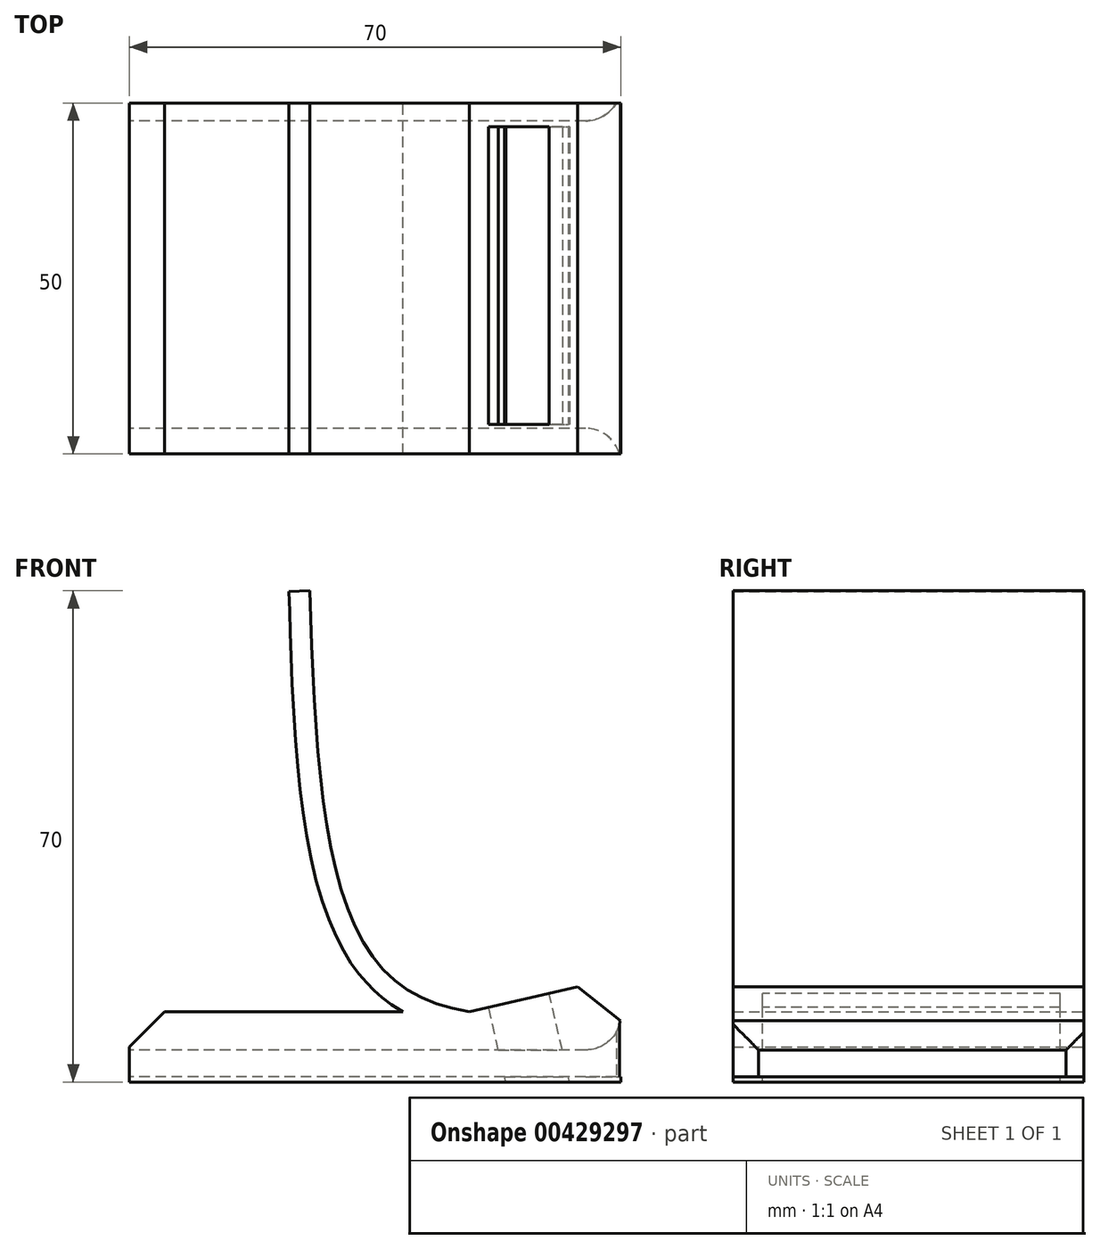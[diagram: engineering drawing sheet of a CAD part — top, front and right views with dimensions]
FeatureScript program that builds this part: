
annotation { "Feature Type Name" : "Feature", "Feature Type Description" : "" }
export const myFeature = defineFeature(function(context is Context, id is Id, definition is map)
    precondition{}
    {
        {
            var Q0;
            Q0=qCreatedBy(makeId("Front.planeOp"),FACE);
            var sketch = newSketch(context, id + "F0", { "sketchPlane" : qUnion([Q0])});
            skLineSegment(sketch, "E0.bottom", {"start": v(0, 0) * mm, "end": v(70, 0) * mm});
            skLineSegment(sketch, "E0.left", {"start": v(0, 0) * mm, "end": v(0, 10) * mm});
            skLineSegment(sketch, "E0.right", {"start": v(70, 0) * mm, "end": v(70, 14.95) * mm});
            skLineSegment(sketch, "E1.top", {"start": v(0, 10) * mm, "end": v(39.04, 10) * mm});
            skLineSegment(sketch, "E1.right", {"start": v(70, 0) * mm, "end": v(70, 10) * mm});
            skFitSpline(sketch, "E2", {"points": [v(70, 10) * mm, v(36.87, 15.29) * mm, v(25.71, 70) * mm], "startDerivative": vector(-88.12, -6.46) * mm, "endDerivative": vector(-4, 121.07) * mm});
            skFitSpline(sketch, "E3.0", {"points": [v(70.22, 7) * mm, v(66.55, 6.74) * mm, v(60.97, 6.33) * mm, v(53.73, 6.36) * mm, v(48.47, 6.84) * mm, v(44.3, 7.77) * mm, v(41.12, 8.94) * mm, v(38.84, 10.06) * mm, v(37.05, 11.22) * mm, v(35.7, 12.28) * mm, v(34.73, 13.16) * mm, v(33.82, 14.1) * mm, v(32.67, 15.43) * mm, v(31.38, 17.24) * mm, v(30.02, 19.61) * mm, v(28.45, 23.01) * mm, v(26.87, 27.67) * mm, v(25.47, 33.83) * mm, v(24.46, 40.48) * mm, v(23.76, 47.5) * mm, v(23.13, 57.26) * mm, v(22.88, 64.86) * mm, v(22.71, 69.9) * mm]});
            skLineSegment(sketch, "E4", {"start": v(22.71, 69.9) * mm, "end": v(25.71, 70) * mm});
            skLineSegment(sketch, "E5", {"start": v(48.4, 10) * mm, "end": v(70, 14.95) * mm});
            skSolve(sketch);
        }
        {
            var Q0;
            Q0 = qSketchRegion(id + "F0", true);
            extrude(context, id + "F1", {"entities" : qUnion([Q0]), "depth" : 50 * mm});
        }
        {
            var Q0;
            Q0=makeQuery(id+"F1.opExtrude","SWEPT_EDGE",EDGE,{"disambiguationData":[OSD([sQuery(id+"F0.wireOp",EDGE,"E1.top"),sQuery(id+"F0.wireOp",EDGE,"E0.left")])]});
            var Q1;
            Q1=makeQuery(id+"F1.opExtrude","SWEPT_EDGE",EDGE,{"disambiguationData":[OSD([sQuery(id+"F0.wireOp",EDGE,"E0.right"),sQuery(id+"F0.wireOp",EDGE,"E5")])]});
            chamfer(context, id + "F2", {"entities" : qUnion([Q0, Q1]), "width" : 5 * mm, "tangentPropagation" : true});
        }
        {
            var Q0;
            Q0=makeQuery(id+"F1.opExtrude","SWEPT_FACE",FACE,{"disambiguationData":[OSD([sQuery(id+"F0.wireOp",EDGE,"E5")])]});
            var sketch = newSketch(context, id + "F3", { "sketchPlane" : qUnion([Q0])});
            skLineSegment(sketch, "E6.bottom", {"start": v(52.26, -3.4) * mm, "end": v(61.13, -3.4) * mm});
            skLineSegment(sketch, "E6.top", {"start": v(52.26, -45.78) * mm, "end": v(61.13, -45.78) * mm});
            skLineSegment(sketch, "E6.left", {"start": v(52.26, -3.4) * mm, "end": v(52.26, -45.78) * mm});
            skLineSegment(sketch, "E6.right", {"start": v(61.13, -3.4) * mm, "end": v(61.13, -45.78) * mm});
            skSolve(sketch);
        }
        {
            var Q0;
            Q0 = qSketchRegion(id + "F3", true);
            extrude(context, id + "F4", {"entities" : qUnion([Q0]), "operationType" : NewBodyOperationType.REMOVE, "oppositeDirection" : true, "depth" : 25 * mm});
        }
        {
            var Q0;
            Q0=makeQuery(id+"F1.opExtrude","SWEPT_FACE",FACE,{"disambiguationData":[OSD([sQuery(id+"F0.wireOp",EDGE,"E0.left")])]});
            var sketch = newSketch(context, id + "F5", { "sketchPlane" : qUnion([Q0])});
            skLineSegment(sketch, "E7.bottom", {"start": v(2.54, 4.57) * mm, "end": v(46.34, 4.57) * mm});
            skLineSegment(sketch, "E7.top", {"start": v(2.54, 0.73) * mm, "end": v(46.34, 0.73) * mm});
            skLineSegment(sketch, "E7.left", {"start": v(2.54, 4.57) * mm, "end": v(2.54, 0.73) * mm});
            skLineSegment(sketch, "E7.right", {"start": v(46.34, 4.57) * mm, "end": v(46.34, 0.73) * mm});
            skSolve(sketch);
        }
        {
            var Q0;
            Q0 = qSketchRegion(id + "F5", true);
            extrude(context, id + "F6", {"entities" : qUnion([Q0]), "operationType" : NewBodyOperationType.REMOVE, "endBound" : BoundingType.THROUGH_ALL, "oppositeDirection" : true, "depth" : 25 * mm});
        }
        {
            var Q0;
            Q0=makeQuery(id+"F6.boolean.opBoolean","INTERSECT",EDGE,{"derivedFrom":[makeQuery(id+"F1.opExtrude","SWEPT_FACE",FACE,{"disambiguationData":[OSD([sQuery(id+"F0.wireOp",EDGE,"E0.right"),sQuery(id+"F0.wireOp",EDGE,"E1.right")])]}),makeQuery(id+"F6.opExtrude","SWEPT_FACE",FACE,{"disambiguationData":[OSD([sQuery(id+"F5.wireOp",EDGE,"E7.right")])]})]});
            var Q1;
            Q1=makeQuery(id+"F6.boolean.opBoolean","INTERSECT",EDGE,{"derivedFrom":[makeQuery(id+"F1.opExtrude","SWEPT_FACE",FACE,{"disambiguationData":[OSD([sQuery(id+"F0.wireOp",EDGE,"E0.right"),sQuery(id+"F0.wireOp",EDGE,"E1.right")])]}),makeQuery(id+"F6.opExtrude","SWEPT_FACE",FACE,{"disambiguationData":[OSD([sQuery(id+"F5.wireOp",EDGE,"E7.left")])]})]});
            var Q2;
            Q2=makeQuery(id+"F6.boolean.opBoolean","INTERSECT",EDGE,{"derivedFrom":[makeQuery(id+"F1.opExtrude","SWEPT_FACE",FACE,{"disambiguationData":[OSD([sQuery(id+"F0.wireOp",EDGE,"E0.right"),sQuery(id+"F0.wireOp",EDGE,"E1.right")])]}),makeQuery(id+"F6.opExtrude","SWEPT_FACE",FACE,{"disambiguationData":[OSD([sQuery(id+"F5.wireOp",EDGE,"E7.bottom")])]})]});
            fillet(context, id + "F7", {"entities" : qUnion([Q0, Q1, Q2]), "radius" : 5 * mm, "tangentPropagation" : true, "allowEdgeOverflow" : false});
        }
    });
